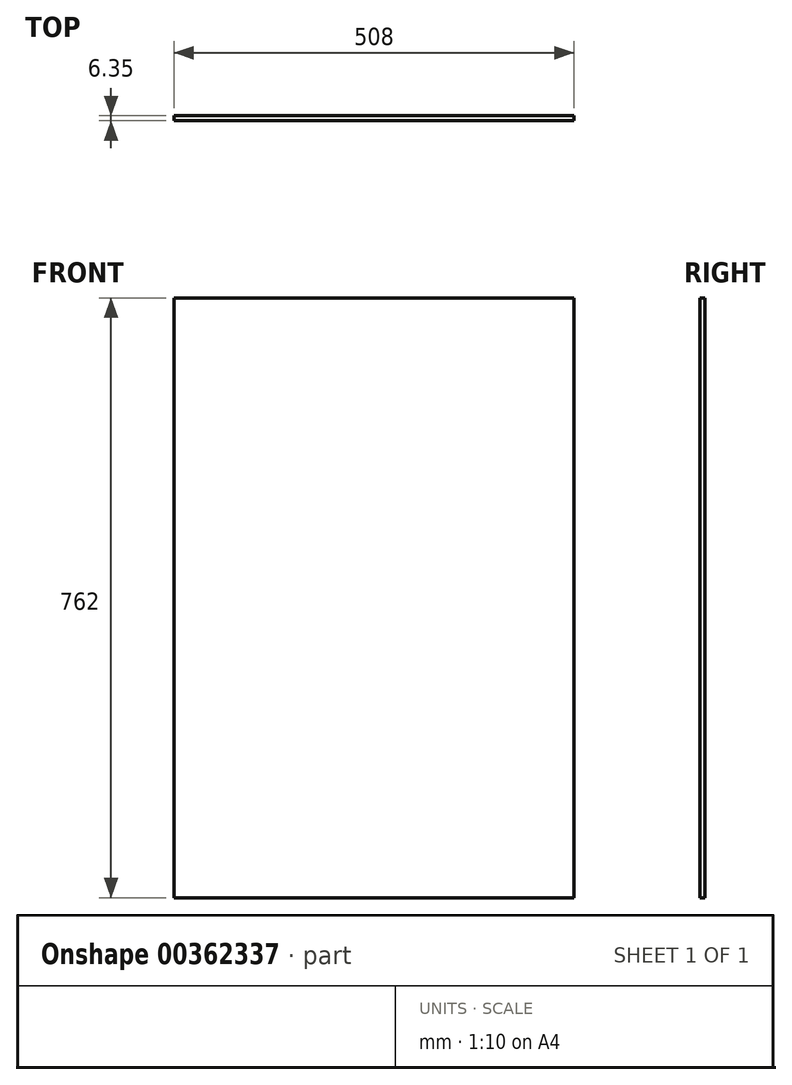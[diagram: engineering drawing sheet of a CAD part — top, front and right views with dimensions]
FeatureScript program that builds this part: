
annotation { "Feature Type Name" : "Feature", "Feature Type Description" : "" }
export const myFeature = defineFeature(function(context is Context, id is Id, definition is map)
    precondition{}
    {
        {
            var Q0;
            Q0=qCreatedBy(makeId("Front.planeOp"),FACE);
            var sketch = newSketch(context, id + "F0", { "sketchPlane" : qUnion([Q0])});
            skLineSegment(sketch, "E0.bottom", {"start": v(-254, 381) * mm, "end": v(254, 381) * mm});
            skLineSegment(sketch, "E0.top", {"start": v(-254, -381) * mm, "end": v(254, -381) * mm});
            skLineSegment(sketch, "E0.left", {"start": v(-254, 381) * mm, "end": v(-254, -381) * mm});
            skLineSegment(sketch, "E0.right", {"start": v(254, 381) * mm, "end": v(254, -381) * mm});
            skPoint(sketch, "E0.middle", {"position": v(0, 0) * mm});
            skSolve(sketch);
        }
        {
            var Q0;
            Q0 = qSketchRegion(id + "F0", true);
            extrude(context, id + "F1", {"entities" : qUnion([Q0]), "depth" : 6.35 * mm});
        }
    });
